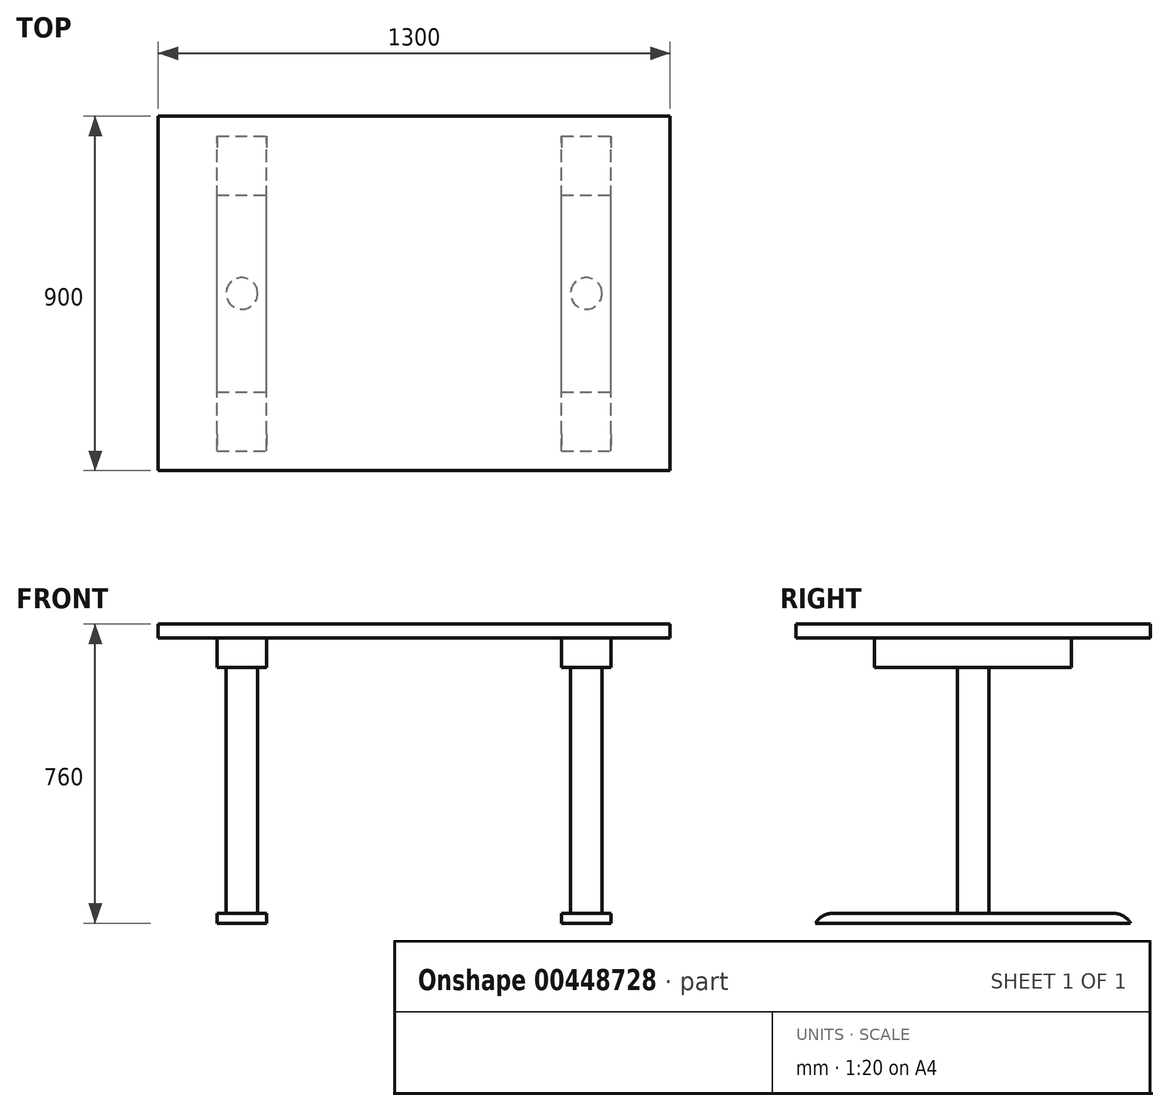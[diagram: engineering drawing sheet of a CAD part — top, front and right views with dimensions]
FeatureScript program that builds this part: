
annotation { "Feature Type Name" : "Feature", "Feature Type Description" : "" }
export const myFeature = defineFeature(function(context is Context, id is Id, definition is map)
    precondition{}
    {
        {
            var Q0;
            Q0=qCreatedBy(makeId("Top.planeOp"),FACE);
            var sketch = newSketch(context, id + "F0", { "sketchPlane" : qUnion([Q0])});
            skLineSegment(sketch, "E0.bottom", {"start": v(-660.76, 523.6) * mm, "end": v(639.24, 523.6) * mm});
            skLineSegment(sketch, "E0.top", {"start": v(-660.76, -376.4) * mm, "end": v(639.24, -376.4) * mm});
            skLineSegment(sketch, "E0.left", {"start": v(-660.76, 523.6) * mm, "end": v(-660.76, -376.4) * mm});
            skLineSegment(sketch, "E0.right", {"start": v(639.24, 523.6) * mm, "end": v(639.24, -376.4) * mm});
            skSolve(sketch);
        }
        {
            var Q0;
            Q0=makeQuery(id+"F0.imprint","IMPRINT",FACE,{"disambiguationData":[TD([[makeQuery(id+"F0.imprint","IMPRINT",EDGE,{"derivedFrom":sQuery(id+"F0.wireOp",EDGE,"E0.bottom")}),-1.0]])]});
            extrude(context, id + "F1", {"entities" : qUnion([Q0]), "depth" : 35 * mm});
        }
        {
            var Q0;
            Q0=makeQuery(id+"F1.opExtrude","CAP_FACE",FACE,{"disambiguationData":[OSD([sQuery(id+"F0.wireOp",EDGE,"E0.bottom"),sQuery(id+"F0.wireOp",EDGE,"E0.top"),sQuery(id+"F0.wireOp",EDGE,"E0.left"),sQuery(id+"F0.wireOp",EDGE,"E0.right")])],"isStart":true});
            var sketch = newSketch(context, id + "F2", { "sketchPlane" : qUnion([Q0])});
            skLineSegment(sketch, "E1.bottom", {"start": v(-510.76, 176.4) * mm, "end": v(-385.76, 176.4) * mm});
            skLineSegment(sketch, "E1.top", {"start": v(-510.76, -323.6) * mm, "end": v(-385.76, -323.6) * mm});
            skLineSegment(sketch, "E1.left", {"start": v(-510.76, 176.4) * mm, "end": v(-510.76, -323.6) * mm});
            skLineSegment(sketch, "E1.right", {"start": v(-385.76, 176.4) * mm, "end": v(-385.76, -323.6) * mm});
            skLineSegment(sketch, "E2.bottom", {"start": v(364.24, 176.4) * mm, "end": v(489.24, 176.4) * mm});
            skLineSegment(sketch, "E2.top", {"start": v(364.24, -323.6) * mm, "end": v(489.24, -323.6) * mm});
            skLineSegment(sketch, "E2.left", {"start": v(364.24, 176.4) * mm, "end": v(364.24, -323.6) * mm});
            skLineSegment(sketch, "E2.right", {"start": v(489.24, 176.4) * mm, "end": v(489.24, -323.6) * mm});
            skSolve(sketch);
        }
        {
            var Q0;
            Q0=makeQuery(id+"F2.imprint","IMPRINT",FACE,{"disambiguationData":[TD([[makeQuery(id+"F2.imprint","IMPRINT",EDGE,{"derivedFrom":sQuery(id+"F2.wireOp",EDGE,"E1.bottom")}),-1.0]])]});
            var Q1;
            Q1=makeQuery(id+"F2.imprint","IMPRINT",FACE,{"disambiguationData":[TD([[makeQuery(id+"F2.imprint","IMPRINT",EDGE,{"derivedFrom":sQuery(id+"F2.wireOp",EDGE,"E2.bottom")}),-1.0]])]});
            extrude(context, id + "F3", {"entities" : qUnion([Q0, Q1]), "operationType" : NewBodyOperationType.ADD, "depth" : 75 * mm});
        }
        {
            var Q0;
            Q0=makeQuery(id+"F3.opExtrude","CAP_FACE",FACE,{"disambiguationData":[OSD([sQuery(id+"F2.wireOp",EDGE,"E1.bottom"),sQuery(id+"F2.wireOp",EDGE,"E1.top"),sQuery(id+"F2.wireOp",EDGE,"E1.left"),sQuery(id+"F2.wireOp",EDGE,"E1.right")])],"isStart":false});
            var sketch = newSketch(context, id + "F4", { "sketchPlane" : qUnion([Q0])});
            skCircle(sketch, "E3", {"center": v(-448.26, -73.6) * mm, "radius": 40 * mm});
            skPoint(sketch, "E3.centerSnap0", {"position": v(-448.26, 176.4) * mm});
            skPoint(sketch, "E3.centerSnap1", {"position": v(-385.76, -73.6) * mm});
            skSolve(sketch);
        }
        {
            var Q0;
            Q0=makeQuery(id+"F3.opExtrude","CAP_FACE",FACE,{"disambiguationData":[OSD([sQuery(id+"F2.wireOp",EDGE,"E2.bottom"),sQuery(id+"F2.wireOp",EDGE,"E2.top"),sQuery(id+"F2.wireOp",EDGE,"E2.left"),sQuery(id+"F2.wireOp",EDGE,"E2.right")])],"isStart":false});
            var sketch = newSketch(context, id + "F5", { "sketchPlane" : qUnion([Q0])});
            skCircle(sketch, "E4", {"center": v(426.74, -73.6) * mm, "radius": 40 * mm});
            skPoint(sketch, "E4.centerSnap0", {"position": v(364.24, -73.6) * mm});
            skPoint(sketch, "E4.centerSnap1", {"position": v(426.74, 176.4) * mm});
            skSolve(sketch);
        }
        {
            var Q0;
            Q0=makeQuery(id+"F4.imprint","IMPRINT",FACE,{"disambiguationData":[TD([[makeQuery(id+"F4.imprint","IMPRINT",EDGE,{"derivedFrom":sQuery(id+"F4.wireOp",EDGE,"E3")}),1.0]])]});
            var Q1;
            Q1=makeQuery(id+"F5.imprint","IMPRINT",FACE,{"disambiguationData":[TD([[makeQuery(id+"F5.imprint","IMPRINT",EDGE,{"derivedFrom":sQuery(id+"F5.wireOp",EDGE,"E4")}),1.0]])]});
            extrude(context, id + "F6", {"entities" : qUnion([Q0, Q1]), "operationType" : NewBodyOperationType.ADD, "depth" : 625 * mm});
        }
        {
            var Q0;
            Q0=makeQuery(id+"F6.opExtrude","CAP_FACE",FACE,{"disambiguationData":[OSD([sQuery(id+"F4.wireOp",EDGE,"E3")])],"isStart":false});
            var sketch = newSketch(context, id + "F7", { "sketchPlane" : qUnion([Q0])});
            skLineSegment(sketch, "E5.bottom", {"start": v(-510.76, 326.4) * mm, "end": v(-385.76, 326.4) * mm});
            skLineSegment(sketch, "E5.top", {"start": v(-510.76, -473.6) * mm, "end": v(-385.76, -473.6) * mm});
            skLineSegment(sketch, "E5.left", {"start": v(-510.76, 326.4) * mm, "end": v(-510.76, -473.6) * mm});
            skLineSegment(sketch, "E5.right", {"start": v(-385.76, 326.4) * mm, "end": v(-385.76, -473.6) * mm});
            skLineSegment(sketch, "E6.bottom", {"start": v(364.24, 326.4) * mm, "end": v(489.24, 326.4) * mm});
            skLineSegment(sketch, "E6.top", {"start": v(364.24, -473.6) * mm, "end": v(489.24, -473.6) * mm});
            skLineSegment(sketch, "E6.left", {"start": v(364.24, 326.4) * mm, "end": v(364.24, -473.6) * mm});
            skLineSegment(sketch, "E6.right", {"start": v(489.24, 326.4) * mm, "end": v(489.24, -473.6) * mm});
            skSolve(sketch);
        }
        {
            var Q0;
            Q0=makeQuery(id+"F7.imprint","IMPRINT",FACE,{"disambiguationData":[TD([[makeQuery(id+"F7.imprint","IMPRINT",EDGE,{"derivedFrom":sQuery(id+"F7.wireOp",EDGE,"E6.bottom")}),-1.0]])]});
            var Q1;
            Q1=makeQuery(id+"F7.imprint","IMPRINT",FACE,{"disambiguationData":[TD([[makeQuery(id+"F7.imprint","IMPRINT",EDGE,{"derivedFrom":makeQuery(id+"F6.opExtrude","CAP_EDGE",EDGE,{"disambiguationData":[OSD([sQuery(id+"F4.wireOp",EDGE,"E3")])],"isStart":false})}),1.0]])]});
            var Q2;
            Q2=makeQuery(id+"F7.imprint","IMPRINT",FACE,{"disambiguationData":[TD([[makeQuery(id+"F7.imprint","IMPRINT",EDGE,{"derivedFrom":sQuery(id+"F7.wireOp",EDGE,"E5.bottom")}),-1.0]])]});
            extrude(context, id + "F8", {"entities" : qUnion([Q0, Q1, Q2]), "operationType" : NewBodyOperationType.ADD, "depth" : 25 * mm});
        }
        {
            var Q0;
            Q0=makeQuery(id+"F8.opExtrude","CAP_EDGE",EDGE,{"disambiguationData":[OSD([sQuery(id+"F7.wireOp",EDGE,"E5.bottom")])],"isStart":true});
            var Q1;
            Q1=makeQuery(id+"F8.opExtrude","CAP_EDGE",EDGE,{"disambiguationData":[OSD([sQuery(id+"F7.wireOp",EDGE,"E5.top")])],"isStart":true});
            var Q2;
            Q2=makeQuery(id+"F8.opExtrude","CAP_EDGE",EDGE,{"disambiguationData":[OSD([sQuery(id+"F7.wireOp",EDGE,"E6.bottom")])],"isStart":true});
            var Q3;
            Q3=makeQuery(id+"F8.opExtrude","CAP_EDGE",EDGE,{"disambiguationData":[OSD([sQuery(id+"F7.wireOp",EDGE,"E6.top")])],"isStart":true});
            fillet(context, id + "F9", {"entities" : qUnion([Q0, Q1, Q2, Q3]), "radius" : 50 * mm, "tangentPropagation" : true, "allowEdgeOverflow" : false});
        }
    });
